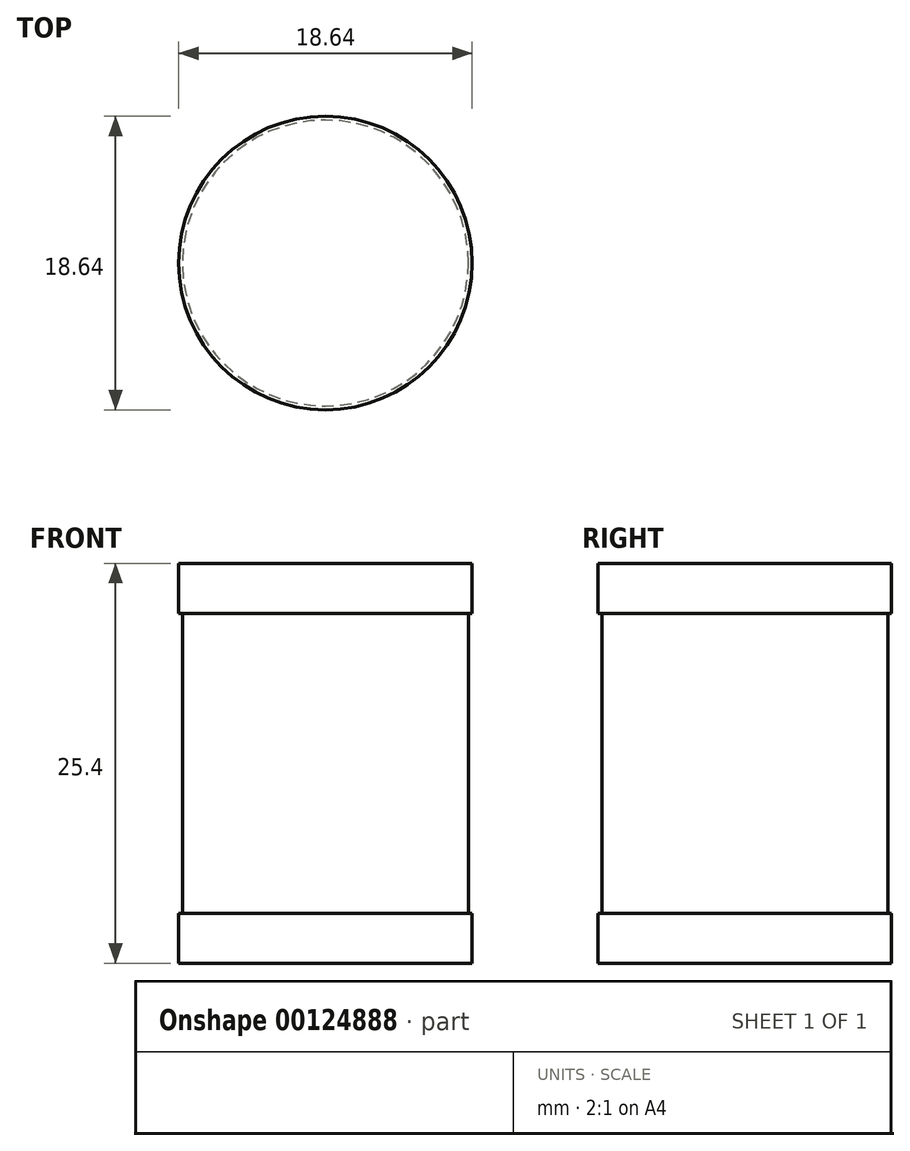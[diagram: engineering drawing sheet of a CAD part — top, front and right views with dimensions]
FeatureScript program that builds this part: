
annotation { "Feature Type Name" : "Feature", "Feature Type Description" : "" }
export const myFeature = defineFeature(function(context is Context, id is Id, definition is map)
    precondition{}
    {
        {
            var Q0;
            Q0=qCreatedBy(makeId("Front.planeOp"),FACE);
            var sketch = newSketch(context, id + "F0", { "sketchPlane" : qUnion([Q0])});
            skLineSegment(sketch, "E0", {"start": v(0, 0) * mm, "end": v(9.32, 0) * mm});
            skLineSegment(sketch, "E1", {"start": v(9.32, 0) * mm, "end": v(9.32, 3.18) * mm});
            skLineSegment(sketch, "E2", {"start": v(9.32, 3.18) * mm, "end": v(9.08, 3.18) * mm});
            skLineSegment(sketch, "E3", {"start": v(9.08, 3.18) * mm, "end": v(9.08, 22.23) * mm});
            skLineSegment(sketch, "E4", {"start": v(9.08, 22.23) * mm, "end": v(9.32, 22.23) * mm});
            skLineSegment(sketch, "E5", {"start": v(9.32, 22.23) * mm, "end": v(9.32, 25.4) * mm});
            skLineSegment(sketch, "E6", {"start": v(9.32, 25.4) * mm, "end": v(0, 25.4) * mm});
            skLineSegment(sketch, "E7", {"start": v(0, 25.4) * mm, "end": v(0, 0) * mm});
            skLineSegment(sketch, "E8", {"start": v(0, 0) * mm, "end": v(0, -3.42) * mm, "construction": true});
            skSolve(sketch);
        }
        {
            var Q0;
            Q0 = qSketchRegion(id + "F0", true);
            var Q1;
            Q1=sQuery(id+"F0.wireOp",EDGE,"E8");
            revolve(context, id + "F1", {"entities" : qUnion([Q0]), "axis" : qUnion([Q1]), "revolveType" : RevolveType.FULL});
        }
    });
